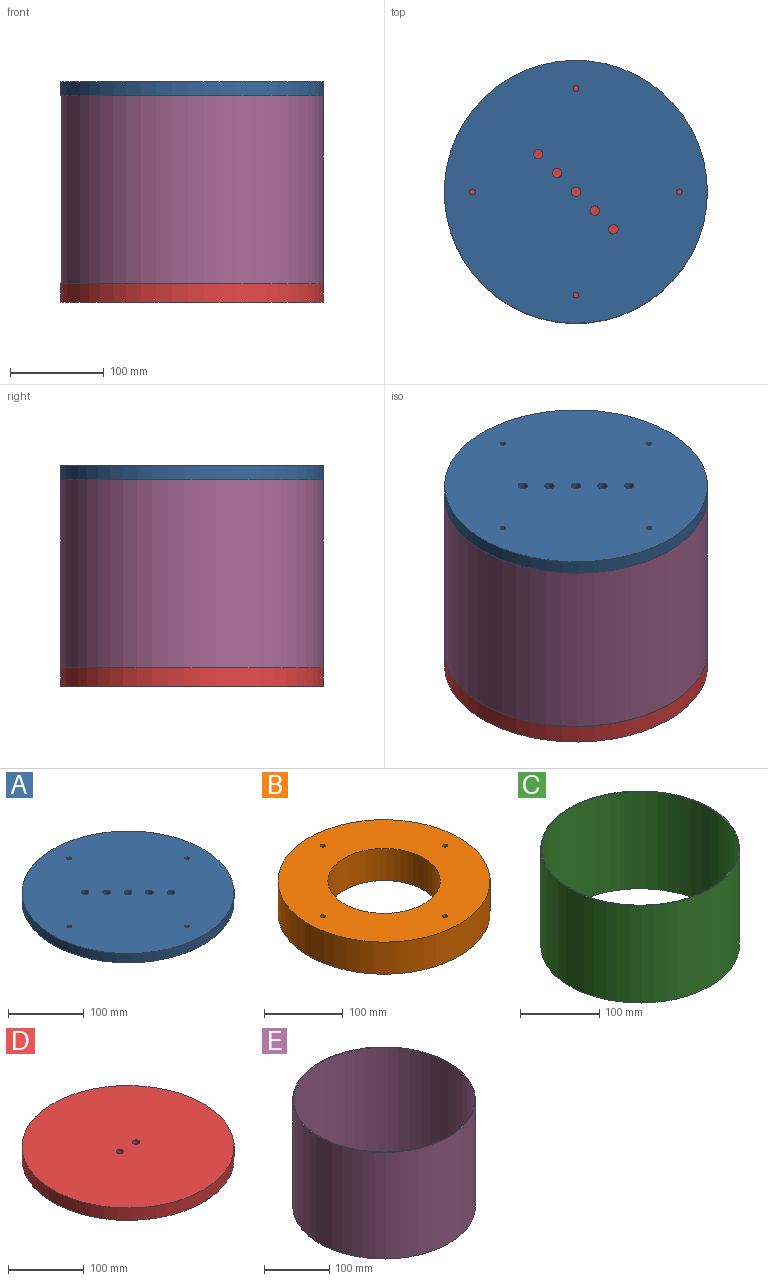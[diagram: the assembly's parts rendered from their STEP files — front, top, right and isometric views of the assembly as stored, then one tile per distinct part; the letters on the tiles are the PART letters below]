
ASSEMBLY  parts=5 mates=6
PART A: 12 faces, bbox 280x280x15 mm
  f0: cylinder r=140mm len=280mm, axis (0,0,-1), area 13194.7mm2, adj f1,f2
  f1: plane 280x280mm, normal (0,0,1), area 61069.4mm2, adj f0,f3,f4,f5,f6,f7,f8,f9
  f2: plane 280x280mm, normal (0,0,-1), area 61069.4mm2, adj f0,f3,f4,f5,f6,f7,f8,f9
  f3: cylinder r=3mm len=15mm, axis (0,0,1), area 282.7mm2, adj f1,f2
  f4: cylinder r=3mm len=15mm, axis (0,0,1), area 282.7mm2, adj f1,f2
  f5: cylinder r=3mm len=15mm, axis (0,0,1), area 282.7mm2, adj f1,f2
  f6: cylinder r=3mm len=15mm, axis (0,0,1), area 282.7mm2, adj f1,f2
  f7: cylinder r=5mm len=15mm, axis (0,0,1), area 471.2mm2, adj f1,f2
  f8: cylinder r=5mm len=15mm, axis (0,0,1), area 471.2mm2, adj f1,f2
  f9: cylinder r=5mm len=15mm, axis (0,0,1), area 471.2mm2, adj f1,f2
  f10: cylinder r=5mm len=15mm, axis (0,0,1), area 471.2mm2, adj f1,f2
  f11: cylinder r=5mm len=15mm, axis (0,0,1), area 471.2mm2, adj f1,f2
PART B: 16 faces, bbox 270x270x50 mm
  f0: cylinder r=71.5mm len=143mm, axis (0,0,-1), area 22462.4mm2, adj f2,f3
  f1: cylinder r=135mm len=270mm, axis (0,0,-1), area 42411.5mm2, adj f2,f3
  f2: plane 270x270mm, normal (0,0,1), area 41081.8mm2, adj f0,f1,f4,f5,f6,f7
  f3: plane 270x270mm, normal (0,0,-1), area 40968.7mm2, adj f0,f1,f4,f5,f6,f7,f8,f10
  f4: cylinder r=3mm len=50mm, axis (0,0,-1), area 942.5mm2, adj f2,f3
  f5: cylinder r=3mm len=50mm, axis (0,0,-1), area 942.5mm2, adj f2,f3
  f6: cylinder r=3mm len=50mm, axis (0,0,1), area 942.5mm2, adj f2,f3
  f7: cylinder r=3mm len=50mm, axis (0,0,1), area 942.5mm2, adj f2,f3
  f8: cylinder r=3mm len=25mm, axis (0,0,-1), area 471.2mm2, adj f3,f9
  f9: plane 6x6mm, normal (0,0,-1), area 28.3mm2, adj f8
  f10: cylinder r=3mm len=25mm, axis (0,0,-1), area 471.2mm2, adj f3,f11
  f11: plane 6x6mm, normal (0,0,-1), area 28.3mm2, adj f10
  f12: cylinder r=3mm len=25mm, axis (0,0,-1), area 471.2mm2, adj f3,f13
  f13: plane 6x6mm, normal (0,0,-1), area 28.3mm2, adj f12
  f14: cylinder r=3mm len=25mm, axis (0,0,-1), area 471.2mm2, adj f3,f15
  f15: plane 6x6mm, normal (0,0,-1), area 28.3mm2, adj f14
PART C: 4 faces, bbox 250x250x150 mm
  f0: cylinder r=125mm len=250mm, axis (0,0,-1), area 117809.7mm2, adj f1,f2
  f1: plane 250x250mm, normal (0,0,1), area 782.3mm2, adj f0,f3
  f2: plane 250x250mm, normal (0,0,-1), area 782.3mm2, adj f0,f3
  f3: cylinder r=124mm len=248mm, axis (0,0,1), area 116867.2mm2, adj f1,f2
PART D: 5 faces, bbox 280x280x20 mm
  f0: cylinder r=140mm len=280mm, axis (0,0,-1), area 17592.9mm2, adj f1,f2
  f1: plane 280x280mm, normal (0,0,1), area 61418.1mm2, adj f0,f3,f4
  f2: plane 280x280mm, normal (0,0,-1), area 61418.1mm2, adj f0,f3,f4
  f3: cylinder r=5mm len=20mm, axis (0,0,1), area 628.3mm2, adj f1,f2
  f4: cylinder r=5mm len=20mm, axis (0,0,1), area 628.3mm2, adj f1,f2
PART E: 4 faces, bbox 280x280x200 mm
  f0: cylinder r=139mm len=278mm, axis (0,0,-1), area 174672.6mm2, adj f2,f3
  f1: cylinder r=140mm len=280mm, axis (0,0,-1), area 175929.2mm2, adj f2,f3
  f2: plane 280x280mm, normal (0,0,1), area 876.5mm2, adj f0,f1
  f3: plane 280x280mm, normal (0,0,-1), area 876.5mm2, adj f0,f1
PLACE A t=(102.93,-191.22,39.24)mm
PLACE B t=(102.93,-191.22,-10.76)mm
PLACE C t=(102.93,-191.22,-160.76)mm
PLACE D t=(102.93,-191.22,-180.76)mm
PLACE E t=(102.93,-191.22,-160.76)mm
MATE parallel B.f1 <-> C.f0  axis (0,0,-1) through (102.93,-191.22,-10.76)mm
MATE parallel A.f0 <-> B.f0  axis (0,0,1) through (102.93,-191.22,54.24)mm
MATE parallel E.f1 <-> A.f7  axis (0,0,1) through (102.93,-191.22,39.24)mm
MATE parallel A.f7 <-> B.f1  axis (0,0,-1) through (102.93,-191.22,39.24)mm
MATE parallel A.f7 <-> B.f1  axis (0,0,-1) through (102.93,-191.22,39.24)mm
MATE parallel D.f0 <-> E.f1  axis (0,0,1) through (102.93,-191.22,-160.76)mm
